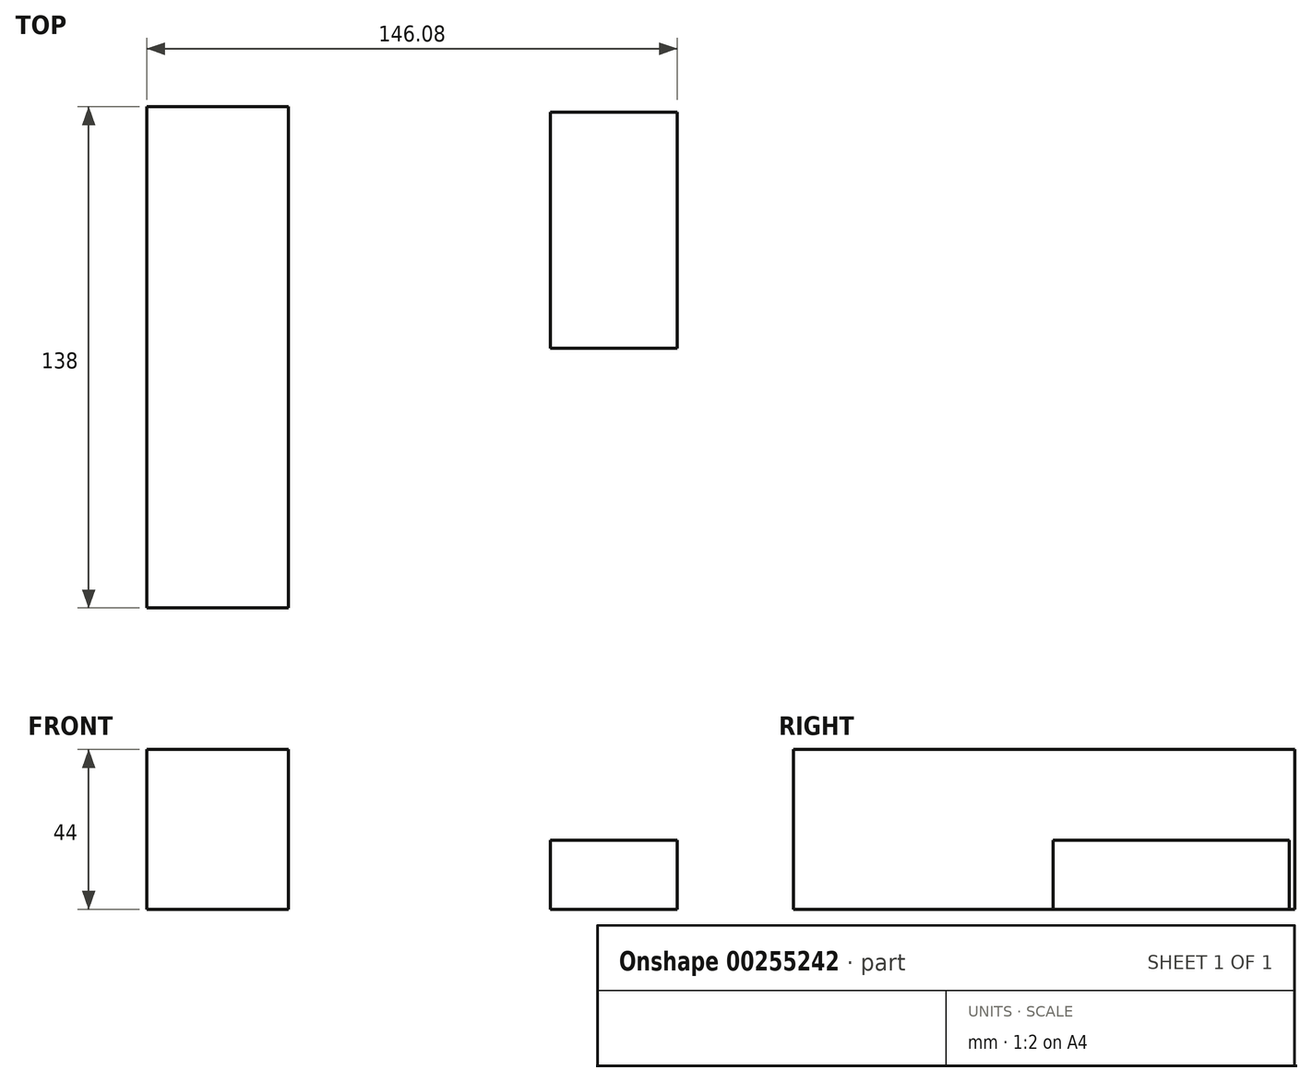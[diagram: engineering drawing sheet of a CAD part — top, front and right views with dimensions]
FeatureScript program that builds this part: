
annotation { "Feature Type Name" : "Feature", "Feature Type Description" : "" }
export const myFeature = defineFeature(function(context is Context, id is Id, definition is map)
    precondition{}
    {
        {
            var Q0;
            Q0=qCreatedBy(makeId("Top.planeOp"),FACE);
            var sketch = newSketch(context, id + "F0", { "sketchPlane" : qUnion([Q0])});
            skLineSegment(sketch, "E0.bottom", {"start": v(-63.71, -61.8) * mm, "end": v(-102.71, -61.8) * mm});
            skLineSegment(sketch, "E0.top", {"start": v(-63.71, 76.2) * mm, "end": v(-102.71, 76.2) * mm});
            skLineSegment(sketch, "E0.left", {"start": v(-63.71, -61.8) * mm, "end": v(-63.71, 76.2) * mm});
            skLineSegment(sketch, "E0.right", {"start": v(-102.71, -61.8) * mm, "end": v(-102.71, 76.2) * mm});
            skPoint(sketch, "E0.middle", {"position": v(-83.21, 7.2) * mm});
            skSolve(sketch);
        }
        {
            var Q0;
            Q0=makeQuery(id+"F0.imprint","IMPRINT",FACE,{"disambiguationData":[TD([[makeQuery(id+"F0.imprint","IMPRINT",EDGE,{"derivedFrom":sQuery(id+"F0.wireOp",EDGE,"E0.bottom")}),-1.0]])]});
            extrude(context, id + "F1", {"entities" : qUnion([Q0]), "depth" : 44 * mm});
        }
        {
            var Q0;
            Q0=qCreatedBy(makeId("Top.planeOp"),FACE);
            var sketch = newSketch(context, id + "F2", { "sketchPlane" : qUnion([Q0])});
            skLineSegment(sketch, "E1.bottom", {"start": v(43.37, 9.66) * mm, "end": v(8.45, 9.66) * mm});
            skLineSegment(sketch, "E1.top", {"start": v(43.37, 74.75) * mm, "end": v(8.45, 74.75) * mm});
            skLineSegment(sketch, "E1.left", {"start": v(43.37, 9.66) * mm, "end": v(43.37, 74.75) * mm});
            skLineSegment(sketch, "E1.right", {"start": v(8.45, 9.66) * mm, "end": v(8.45, 74.75) * mm});
            skPoint(sketch, "E1.middle", {"position": v(25.9, 42.2) * mm});
            skSolve(sketch);
        }
        {
            var Q0;
            Q0=makeQuery(id+"F2.imprint","IMPRINT",FACE,{"disambiguationData":[TD([[makeQuery(id+"F2.imprint","IMPRINT",EDGE,{"derivedFrom":sQuery(id+"F2.wireOp",EDGE,"E1.bottom")}),-1.0]])]});
            extrude(context, id + "F3", {"entities" : qUnion([Q0]), "depth" : 19.05 * mm});
        }
    });
